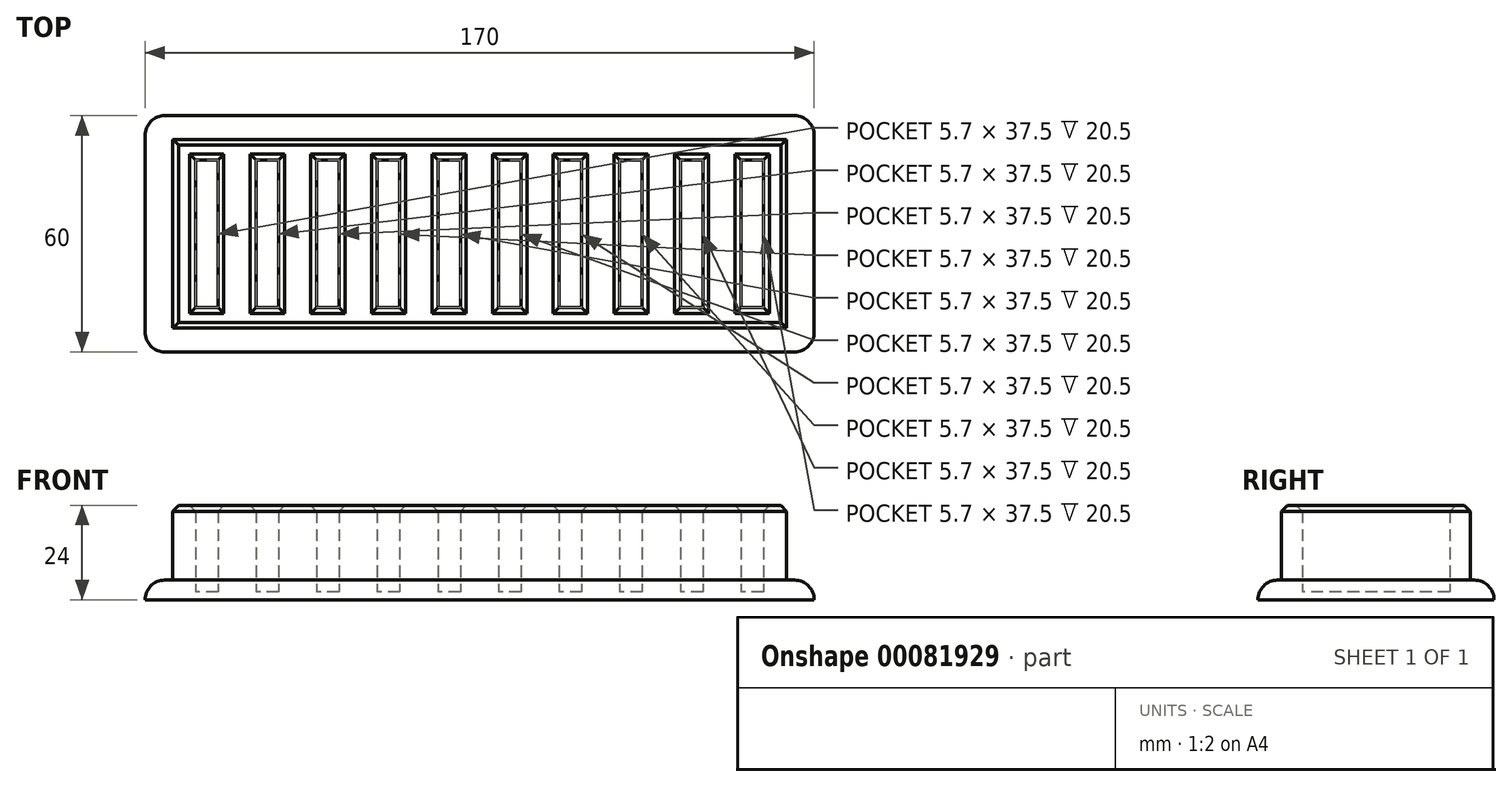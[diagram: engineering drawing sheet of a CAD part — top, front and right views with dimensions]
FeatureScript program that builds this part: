
annotation { "Feature Type Name" : "Feature", "Feature Type Description" : "" }
export const myFeature = defineFeature(function(context is Context, id is Id, definition is map)
    precondition{}
    {
        {
            var Q0;
            Q0=qCreatedBy(makeId("Top.planeOp"),FACE);
            var sketch = newSketch(context, id + "F0", { "sketchPlane" : qUnion([Q0])});
            skLineSegment(sketch, "E0.rect.bottom", {"start": v(78, 24) * mm, "end": v(-78, 24) * mm});
            skLineSegment(sketch, "E0.rect.top", {"start": v(78, -24) * mm, "end": v(-78, -24) * mm});
            skLineSegment(sketch, "E0.rect.left", {"start": v(78, 24) * mm, "end": v(78, -24) * mm});
            skLineSegment(sketch, "E0.rect.right", {"start": v(-78, 24) * mm, "end": v(-78, -24) * mm});
            skPoint(sketch, "E0.rect.middle", {"position": v(0, 0) * mm});
            skLineSegment(sketch, "E1.rect.bottom", {"start": v(-85, 30) * mm, "end": v(85, 30) * mm});
            skLineSegment(sketch, "E1.rect.top", {"start": v(-85, -30) * mm, "end": v(85, -30) * mm});
            skLineSegment(sketch, "E1.rect.left", {"start": v(-85, 30) * mm, "end": v(-85, -30) * mm});
            skLineSegment(sketch, "E1.rect.right", {"start": v(85, 30) * mm, "end": v(85, -30) * mm});
            skSolve(sketch);
        }
        {
            var Q0;
            Q0=makeQuery(id+"F0.imprint","IMPRINT",FACE,{"disambiguationData":[TD([[makeQuery(id+"F0.imprint","IMPRINT",EDGE,{"derivedFrom":sQuery(id+"F0.wireOp",EDGE,"E0.rect.bottom")}),1.0]])]});
            extrude(context, id + "F1", {"entities" : qUnion([Q0]), "depth" : 2 * mm});
        }
        {
            var Q0;
            Q0=makeQuery(id+"F1.opExtrude","CAP_FACE",FACE,{"disambiguationData":[OSD([sQuery(id+"F0.wireOp",EDGE,"E0.rect.bottom"),sQuery(id+"F0.wireOp",EDGE,"E0.rect.top"),sQuery(id+"F0.wireOp",EDGE,"E0.rect.left"),sQuery(id+"F0.wireOp",EDGE,"E0.rect.right")])],"isStart":false});
            var sketch = newSketch(context, id + "F2", { "sketchPlane" : qUnion([Q0])});
            skLineSegment(sketch, "E2.rect.bottom", {"start": v(-66.5, 18.75) * mm, "end": v(-72.2, 18.75) * mm});
            skLineSegment(sketch, "E2.rect.top", {"start": v(-66.5, -18.75) * mm, "end": v(-72.2, -18.75) * mm});
            skLineSegment(sketch, "E2.rect.left", {"start": v(-66.5, 18.75) * mm, "end": v(-66.5, -18.75) * mm});
            skLineSegment(sketch, "E2.rect.right", {"start": v(-72.2, 18.75) * mm, "end": v(-72.2, -18.75) * mm});
            skPoint(sketch, "E2.rect.middle", {"position": v(-69.35, 0) * mm});
            skLineSegment(sketch, "E3.1.0.0", {"start": v(-51.1, 18.75) * mm, "end": v(-51.1, -18.75) * mm});
            skLineSegment(sketch, "E3.1.0.1", {"start": v(-56.8, 18.75) * mm, "end": v(-56.8, -18.75) * mm});
            skLineSegment(sketch, "E3.1.0.2", {"start": v(-51.1, 18.75) * mm, "end": v(-56.8, 18.75) * mm});
            skLineSegment(sketch, "E3.1.0.3", {"start": v(-51.1, -18.75) * mm, "end": v(-56.8, -18.75) * mm});
            skLineSegment(sketch, "E3.2.0.0", {"start": v(-35.7, 18.75) * mm, "end": v(-35.7, -18.75) * mm});
            skLineSegment(sketch, "E3.2.0.1", {"start": v(-41.4, 18.75) * mm, "end": v(-41.4, -18.75) * mm});
            skLineSegment(sketch, "E3.2.0.2", {"start": v(-35.7, 18.75) * mm, "end": v(-41.4, 18.75) * mm});
            skLineSegment(sketch, "E3.2.0.3", {"start": v(-35.7, -18.75) * mm, "end": v(-41.4, -18.75) * mm});
            skLineSegment(sketch, "E3.3.0.0", {"start": v(-20.3, 18.75) * mm, "end": v(-20.3, -18.75) * mm});
            skLineSegment(sketch, "E3.3.0.1", {"start": v(-26, 18.75) * mm, "end": v(-26, -18.75) * mm});
            skLineSegment(sketch, "E3.3.0.2", {"start": v(-20.3, 18.75) * mm, "end": v(-26, 18.75) * mm});
            skLineSegment(sketch, "E3.3.0.3", {"start": v(-20.3, -18.75) * mm, "end": v(-26, -18.75) * mm});
            skLineSegment(sketch, "E3.4.0.0", {"start": v(-4.9, 18.75) * mm, "end": v(-4.9, -18.75) * mm});
            skLineSegment(sketch, "E3.4.0.1", {"start": v(-10.6, 18.75) * mm, "end": v(-10.6, -18.75) * mm});
            skLineSegment(sketch, "E3.4.0.2", {"start": v(-4.9, 18.75) * mm, "end": v(-10.6, 18.75) * mm});
            skLineSegment(sketch, "E3.4.0.3", {"start": v(-4.9, -18.75) * mm, "end": v(-10.6, -18.75) * mm});
            skLineSegment(sketch, "E3.5.0.0", {"start": v(10.5, 18.75) * mm, "end": v(10.5, -18.75) * mm});
            skLineSegment(sketch, "E3.5.0.1", {"start": v(4.8, 18.75) * mm, "end": v(4.8, -18.75) * mm});
            skLineSegment(sketch, "E3.5.0.2", {"start": v(10.5, 18.75) * mm, "end": v(4.8, 18.75) * mm});
            skLineSegment(sketch, "E3.5.0.3", {"start": v(10.5, -18.75) * mm, "end": v(4.8, -18.75) * mm});
            skLineSegment(sketch, "E3.6.0.0", {"start": v(25.9, 18.75) * mm, "end": v(25.9, -18.75) * mm});
            skLineSegment(sketch, "E3.6.0.1", {"start": v(20.2, 18.75) * mm, "end": v(20.2, -18.75) * mm});
            skLineSegment(sketch, "E3.6.0.2", {"start": v(25.9, 18.75) * mm, "end": v(20.2, 18.75) * mm});
            skLineSegment(sketch, "E3.6.0.3", {"start": v(25.9, -18.75) * mm, "end": v(20.2, -18.75) * mm});
            skLineSegment(sketch, "E3.7.0.0", {"start": v(41.3, 18.75) * mm, "end": v(41.3, -18.75) * mm});
            skLineSegment(sketch, "E3.7.0.1", {"start": v(35.6, 18.75) * mm, "end": v(35.6, -18.75) * mm});
            skLineSegment(sketch, "E3.7.0.2", {"start": v(41.3, 18.75) * mm, "end": v(35.6, 18.75) * mm});
            skLineSegment(sketch, "E3.7.0.3", {"start": v(41.3, -18.75) * mm, "end": v(35.6, -18.75) * mm});
            skLineSegment(sketch, "E3.8.0.0", {"start": v(56.7, 18.75) * mm, "end": v(56.7, -18.75) * mm});
            skLineSegment(sketch, "E3.8.0.1", {"start": v(51, 18.75) * mm, "end": v(51, -18.75) * mm});
            skLineSegment(sketch, "E3.8.0.2", {"start": v(56.7, 18.75) * mm, "end": v(51, 18.75) * mm});
            skLineSegment(sketch, "E3.8.0.3", {"start": v(56.7, -18.75) * mm, "end": v(51, -18.75) * mm});
            skLineSegment(sketch, "E3.9.0.0", {"start": v(72.1, 18.75) * mm, "end": v(72.1, -18.75) * mm});
            skLineSegment(sketch, "E3.9.0.1", {"start": v(66.4, 18.75) * mm, "end": v(66.4, -18.75) * mm});
            skLineSegment(sketch, "E3.9.0.2", {"start": v(72.1, 18.75) * mm, "end": v(66.4, 18.75) * mm});
            skLineSegment(sketch, "E3.9.0.3", {"start": v(72.1, -18.75) * mm, "end": v(66.4, -18.75) * mm});
            skLineSegment(sketch, "E3.direction1", {"start": v(-72.2, -18.75) * mm, "end": v(-56.8, -18.75) * mm, "construction": true});
            skSolve(sketch);
        }
        {
            var Q0;
            Q0=makeQuery(id+"F2.imprint","IMPRINT",FACE,{"disambiguationData":[TD([[makeQuery(id+"F2.imprint","IMPRINT",EDGE,{"derivedFrom":sQuery(id+"F2.wireOp",EDGE,"E2.rect.bottom")}),-1.0]])]});
            extrude(context, id + "F3", {"entities" : qUnion([Q0]), "operationType" : NewBodyOperationType.ADD, "depth" : 22 * mm});
        }
        {
            var Q0;
            Q0=makeQuery(id+"F0.imprint","IMPRINT",FACE,{"disambiguationData":[TD([[makeQuery(id+"F0.imprint","IMPRINT",EDGE,{"derivedFrom":sQuery(id+"F0.wireOp",EDGE,"E0.rect.bottom")}),-1.0]])]});
            extrude(context, id + "F4", {"entities" : qUnion([Q0]), "operationType" : NewBodyOperationType.ADD, "depth" : 5 * mm});
        }
        {
            var Q0;
            Q0=makeQuery(id+"F4.opExtrude","CAP_EDGE",EDGE,{"disambiguationData":[OSD([sQuery(id+"F0.wireOp",EDGE,"E1.rect.top")])],"isStart":false});
            var Q1;
            Q1=makeQuery(id+"F4.opExtrude","CAP_EDGE",EDGE,{"disambiguationData":[OSD([sQuery(id+"F0.wireOp",EDGE,"E1.rect.left")])],"isStart":false});
            var Q2;
            Q2=makeQuery(id+"F4.opExtrude","CAP_EDGE",EDGE,{"disambiguationData":[OSD([sQuery(id+"F0.wireOp",EDGE,"E1.rect.bottom")])],"isStart":false});
            var Q3;
            Q3=makeQuery(id+"F4.opExtrude","CAP_EDGE",EDGE,{"disambiguationData":[OSD([sQuery(id+"F0.wireOp",EDGE,"E1.rect.right")])],"isStart":false});
            var Q4;
            Q4=makeQuery(id+"F4.opExtrude","SWEPT_EDGE",EDGE,{"disambiguationData":[OSD([sQuery(id+"F0.wireOp",EDGE,"E1.rect.top"),sQuery(id+"F0.wireOp",EDGE,"E1.rect.right")])]});
            var Q5;
            Q5=makeQuery(id+"F4.opExtrude","SWEPT_EDGE",EDGE,{"disambiguationData":[OSD([sQuery(id+"F0.wireOp",EDGE,"E1.rect.bottom"),sQuery(id+"F0.wireOp",EDGE,"E1.rect.right")])]});
            var Q6;
            Q6=makeQuery(id+"F4.opExtrude","SWEPT_EDGE",EDGE,{"disambiguationData":[OSD([sQuery(id+"F0.wireOp",EDGE,"E1.rect.top"),sQuery(id+"F0.wireOp",EDGE,"E1.rect.left")])]});
            var Q7;
            Q7=makeQuery(id+"F4.opExtrude","SWEPT_EDGE",EDGE,{"disambiguationData":[OSD([sQuery(id+"F0.wireOp",EDGE,"E1.rect.bottom"),sQuery(id+"F0.wireOp",EDGE,"E1.rect.left")])]});
            fillet(context, id + "F5", {"entities" : qUnion([Q0, Q1, Q2, Q3, Q4, Q5, Q6, Q7]), "radius" : 5 * mm, "tangentPropagation" : true, "allowEdgeOverflow" : false});
        }
        {
            var Q0;
            Q0=makeQuery(id+"F3.opExtrude","CAP_EDGE",EDGE,{"disambiguationData":[OSD([sQuery(id+"F0.wireOp",EDGE,"E0.rect.top")])],"isStart":false});
            var Q1;
            Q1=makeQuery(id+"F3.opExtrude","CAP_EDGE",EDGE,{"disambiguationData":[OSD([sQuery(id+"F0.wireOp",EDGE,"E0.rect.right")])],"isStart":false});
            var Q2;
            Q2=makeQuery(id+"F3.opExtrude","CAP_EDGE",EDGE,{"disambiguationData":[OSD([sQuery(id+"F0.wireOp",EDGE,"E0.rect.bottom")])],"isStart":false});
            var Q3;
            Q3=makeQuery(id+"F3.opExtrude","CAP_EDGE",EDGE,{"disambiguationData":[OSD([sQuery(id+"F0.wireOp",EDGE,"E0.rect.left")])],"isStart":false});
            var Q4;
            Q4=makeQuery(id+"F3.opExtrude","CAP_EDGE",EDGE,{"disambiguationData":[OSD([sQuery(id+"F2.wireOp",EDGE,"E2.rect.right")])],"isStart":false});
            var Q5;
            Q5=makeQuery(id+"F3.opExtrude","CAP_EDGE",EDGE,{"disambiguationData":[OSD([sQuery(id+"F2.wireOp",EDGE,"E2.rect.left")])],"isStart":false});
            var Q6;
            Q6=makeQuery(id+"F3.opExtrude","CAP_EDGE",EDGE,{"disambiguationData":[OSD([sQuery(id+"F2.wireOp",EDGE,"E2.rect.top")])],"isStart":false});
            var Q7;
            Q7=makeQuery(id+"F3.opExtrude","CAP_EDGE",EDGE,{"disambiguationData":[OSD([sQuery(id+"F2.wireOp",EDGE,"E2.rect.bottom")])],"isStart":false});
            var Q8;
            Q8=makeQuery(id+"F3.opExtrude","CAP_EDGE",EDGE,{"disambiguationData":[OSD([sQuery(id+"F2.wireOp",EDGE,"E3.1.0.3")])],"isStart":false});
            var Q9;
            Q9=makeQuery(id+"F3.opExtrude","CAP_EDGE",EDGE,{"disambiguationData":[OSD([sQuery(id+"F2.wireOp",EDGE,"E3.1.0.0")])],"isStart":false});
            var Q10;
            Q10=makeQuery(id+"F3.opExtrude","CAP_EDGE",EDGE,{"disambiguationData":[OSD([sQuery(id+"F2.wireOp",EDGE,"E3.1.0.1")])],"isStart":false});
            var Q11;
            Q11=makeQuery(id+"F3.opExtrude","CAP_EDGE",EDGE,{"disambiguationData":[OSD([sQuery(id+"F2.wireOp",EDGE,"E3.1.0.2")])],"isStart":false});
            var Q12;
            Q12=makeQuery(id+"F3.opExtrude","CAP_EDGE",EDGE,{"disambiguationData":[OSD([sQuery(id+"F2.wireOp",EDGE,"E3.2.0.2")])],"isStart":false});
            var Q13;
            Q13=makeQuery(id+"F3.opExtrude","CAP_EDGE",EDGE,{"disambiguationData":[OSD([sQuery(id+"F2.wireOp",EDGE,"E3.2.0.1")])],"isStart":false});
            var Q14;
            Q14=makeQuery(id+"F3.opExtrude","CAP_EDGE",EDGE,{"disambiguationData":[OSD([sQuery(id+"F2.wireOp",EDGE,"E3.2.0.3")])],"isStart":false});
            var Q15;
            Q15=makeQuery(id+"F3.opExtrude","CAP_EDGE",EDGE,{"disambiguationData":[OSD([sQuery(id+"F2.wireOp",EDGE,"E3.2.0.0")])],"isStart":false});
            var Q16;
            Q16=makeQuery(id+"F3.opExtrude","CAP_EDGE",EDGE,{"disambiguationData":[OSD([sQuery(id+"F2.wireOp",EDGE,"E3.3.0.1")])],"isStart":false});
            var Q17;
            Q17=makeQuery(id+"F3.opExtrude","CAP_EDGE",EDGE,{"disambiguationData":[OSD([sQuery(id+"F2.wireOp",EDGE,"E3.3.0.0")])],"isStart":false});
            var Q18;
            Q18=makeQuery(id+"F3.opExtrude","CAP_EDGE",EDGE,{"disambiguationData":[OSD([sQuery(id+"F2.wireOp",EDGE,"E3.3.0.3")])],"isStart":false});
            var Q19;
            Q19=makeQuery(id+"F3.opExtrude","CAP_EDGE",EDGE,{"disambiguationData":[OSD([sQuery(id+"F2.wireOp",EDGE,"E3.3.0.2")])],"isStart":false});
            var Q20;
            Q20=makeQuery(id+"F3.opExtrude","CAP_EDGE",EDGE,{"disambiguationData":[OSD([sQuery(id+"F2.wireOp",EDGE,"E3.4.0.1")])],"isStart":false});
            var Q21;
            Q21=makeQuery(id+"F3.opExtrude","CAP_EDGE",EDGE,{"disambiguationData":[OSD([sQuery(id+"F2.wireOp",EDGE,"E3.4.0.2")])],"isStart":false});
            var Q22;
            Q22=makeQuery(id+"F3.opExtrude","CAP_EDGE",EDGE,{"disambiguationData":[OSD([sQuery(id+"F2.wireOp",EDGE,"E3.4.0.0")])],"isStart":false});
            var Q23;
            Q23=makeQuery(id+"F3.opExtrude","CAP_EDGE",EDGE,{"disambiguationData":[OSD([sQuery(id+"F2.wireOp",EDGE,"E3.4.0.3")])],"isStart":false});
            var Q24;
            Q24=makeQuery(id+"F3.opExtrude","CAP_EDGE",EDGE,{"disambiguationData":[OSD([sQuery(id+"F2.wireOp",EDGE,"E3.5.0.3")])],"isStart":false});
            var Q25;
            Q25=makeQuery(id+"F3.opExtrude","CAP_EDGE",EDGE,{"disambiguationData":[OSD([sQuery(id+"F2.wireOp",EDGE,"E3.5.0.1")])],"isStart":false});
            var Q26;
            Q26=makeQuery(id+"F3.opExtrude","CAP_EDGE",EDGE,{"disambiguationData":[OSD([sQuery(id+"F2.wireOp",EDGE,"E3.5.0.0")])],"isStart":false});
            var Q27;
            Q27=makeQuery(id+"F3.opExtrude","CAP_EDGE",EDGE,{"disambiguationData":[OSD([sQuery(id+"F2.wireOp",EDGE,"E3.5.0.2")])],"isStart":false});
            var Q28;
            Q28=makeQuery(id+"F3.opExtrude","CAP_EDGE",EDGE,{"disambiguationData":[OSD([sQuery(id+"F2.wireOp",EDGE,"E3.6.0.1")])],"isStart":false});
            var Q29;
            Q29=makeQuery(id+"F3.opExtrude","CAP_EDGE",EDGE,{"disambiguationData":[OSD([sQuery(id+"F2.wireOp",EDGE,"E3.6.0.2")])],"isStart":false});
            var Q30;
            Q30=makeQuery(id+"F3.opExtrude","CAP_EDGE",EDGE,{"disambiguationData":[OSD([sQuery(id+"F2.wireOp",EDGE,"E3.6.0.0")])],"isStart":false});
            var Q31;
            Q31=makeQuery(id+"F3.opExtrude","CAP_EDGE",EDGE,{"disambiguationData":[OSD([sQuery(id+"F2.wireOp",EDGE,"E3.6.0.3")])],"isStart":false});
            var Q32;
            Q32=makeQuery(id+"F3.opExtrude","CAP_EDGE",EDGE,{"disambiguationData":[OSD([sQuery(id+"F2.wireOp",EDGE,"E3.7.0.3")])],"isStart":false});
            var Q33;
            Q33=makeQuery(id+"F3.opExtrude","CAP_EDGE",EDGE,{"disambiguationData":[OSD([sQuery(id+"F2.wireOp",EDGE,"E3.7.0.1")])],"isStart":false});
            var Q34;
            Q34=makeQuery(id+"F3.opExtrude","CAP_EDGE",EDGE,{"disambiguationData":[OSD([sQuery(id+"F2.wireOp",EDGE,"E3.7.0.0")])],"isStart":false});
            var Q35;
            Q35=makeQuery(id+"F3.opExtrude","CAP_EDGE",EDGE,{"disambiguationData":[OSD([sQuery(id+"F2.wireOp",EDGE,"E3.7.0.2")])],"isStart":false});
            var Q36;
            Q36=makeQuery(id+"F3.opExtrude","CAP_EDGE",EDGE,{"disambiguationData":[OSD([sQuery(id+"F2.wireOp",EDGE,"E3.8.0.1")])],"isStart":false});
            var Q37;
            Q37=makeQuery(id+"F3.opExtrude","CAP_EDGE",EDGE,{"disambiguationData":[OSD([sQuery(id+"F2.wireOp",EDGE,"E3.8.0.3")])],"isStart":false});
            var Q38;
            Q38=makeQuery(id+"F3.opExtrude","CAP_EDGE",EDGE,{"disambiguationData":[OSD([sQuery(id+"F2.wireOp",EDGE,"E3.8.0.0")])],"isStart":false});
            var Q39;
            Q39=makeQuery(id+"F3.opExtrude","CAP_EDGE",EDGE,{"disambiguationData":[OSD([sQuery(id+"F2.wireOp",EDGE,"E3.8.0.2")])],"isStart":false});
            var Q40;
            Q40=makeQuery(id+"F3.opExtrude","CAP_EDGE",EDGE,{"disambiguationData":[OSD([sQuery(id+"F2.wireOp",EDGE,"E3.9.0.1")])],"isStart":false});
            var Q41;
            Q41=makeQuery(id+"F3.opExtrude","CAP_EDGE",EDGE,{"disambiguationData":[OSD([sQuery(id+"F2.wireOp",EDGE,"E3.9.0.3")])],"isStart":false});
            var Q42;
            Q42=makeQuery(id+"F3.opExtrude","CAP_EDGE",EDGE,{"disambiguationData":[OSD([sQuery(id+"F2.wireOp",EDGE,"E3.9.0.0")])],"isStart":false});
            var Q43;
            Q43=makeQuery(id+"F3.opExtrude","CAP_EDGE",EDGE,{"disambiguationData":[OSD([sQuery(id+"F2.wireOp",EDGE,"E3.9.0.2")])],"isStart":false});
            chamfer(context, id + "F6", {"entities" : qUnion([Q0, Q1, Q2, Q3, Q4, Q5, Q6, Q7, Q8, Q9, Q10, Q11, Q12, Q13, Q14, Q15, Q16, Q17, Q18, Q19, Q20, Q21, Q22, Q23, Q24, Q25, Q26, Q27, Q28, Q29, Q30, Q31, Q32, Q33, Q34, Q35, Q36, Q37, Q38, Q39, Q40, Q41, Q42, Q43]), "width" : 1.5 * mm, "tangentPropagation" : true});
        }
    });
